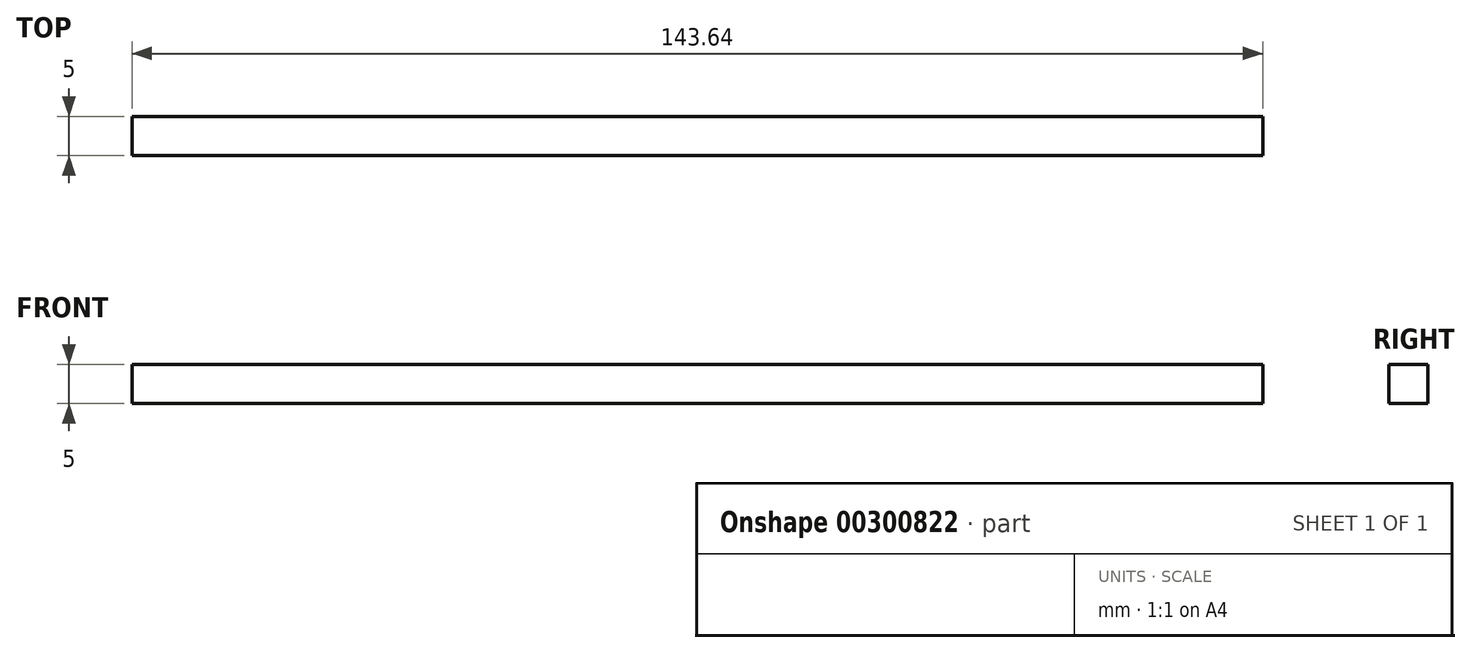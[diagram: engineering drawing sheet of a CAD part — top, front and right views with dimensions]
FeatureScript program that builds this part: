
annotation { "Feature Type Name" : "Feature", "Feature Type Description" : "" }
export const myFeature = defineFeature(function(context is Context, id is Id, definition is map)
    precondition{}
    {
        {
            var Q0;
            Q0=qCreatedBy(makeId("Top.planeOp"),FACE);
            var sketch = newSketch(context, id + "F0", { "sketchPlane" : qUnion([Q0])});
            skLineSegment(sketch, "E0", {"start": v(0, 2.5) * mm, "end": v(-71.82, 2.5) * mm});
            skLineSegment(sketch, "E1.MirrorCS", {"start": v(0, -2.5) * mm, "end": v(-71.82, -2.5) * mm});
            skLineSegment(sketch, "E2.MirrorCS", {"start": v(0, 2.5) * mm, "end": v(71.82, 2.5) * mm});
            skLineSegment(sketch, "E3.MirrorCS", {"start": v(0, -2.5) * mm, "end": v(71.82, -2.5) * mm});
            skLineSegment(sketch, "E4", {"start": v(-71.82, 2.5) * mm, "end": v(-71.82, -2.5) * mm});
            skLineSegment(sketch, "E5", {"start": v(71.82, -2.5) * mm, "end": v(71.82, 2.5) * mm});
            skSolve(sketch);
        }
        {
            var Q0;
            Q0 = qSketchRegion(id + "F0", true);
            extrude(context, id + "F1", {"entities" : qUnion([Q0]), "depth" : 5 * mm});
        }
    });
